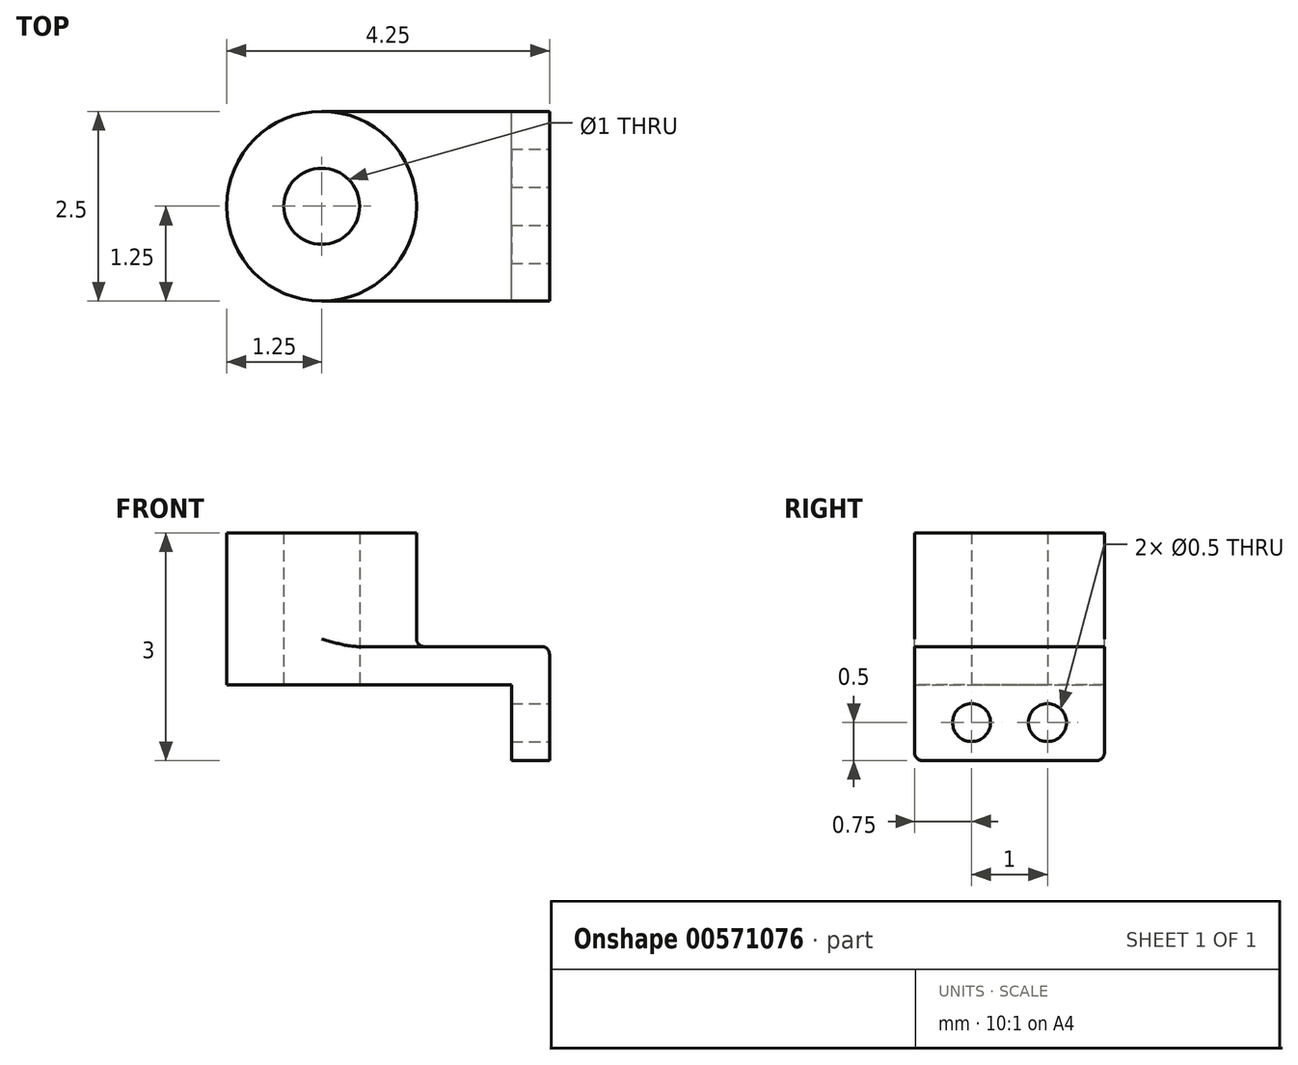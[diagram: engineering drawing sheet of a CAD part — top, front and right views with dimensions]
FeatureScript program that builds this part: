
annotation { "Feature Type Name" : "Feature", "Feature Type Description" : "" }
export const myFeature = defineFeature(function(context is Context, id is Id, definition is map)
    precondition{}
    {
        {
            var Q0;
            Q0=qCreatedBy(makeId("Top.planeOp"),FACE);
            var sketch = newSketch(context, id + "F0", { "sketchPlane" : qUnion([Q0])});
            skLineSegment(sketch, "E0.bottom", {"start": v(1.5, -1.25) * mm, "end": v(-1.5, -1.25) * mm});
            skLineSegment(sketch, "E0.top", {"start": v(1.5, 1.25) * mm, "end": v(-1.5, 1.25) * mm});
            skLineSegment(sketch, "E0.left", {"start": v(1.5, -1.25) * mm, "end": v(1.5, 1.25) * mm});
            skLineSegment(sketch, "E0.right", {"start": v(-1.5, -1.25) * mm, "end": v(-1.5, 1.25) * mm});
            skPoint(sketch, "E0.middle", {"position": v(0, 0) * mm});
            skCircle(sketch, "E1", {"center": v(-1.5, 0) * mm, "radius": 1.25 * mm});
            skCircle(sketch, "E2", {"center": v(-1.5, 0) * mm, "radius": 0.5 * mm});
            skSolve(sketch);
        }
        {
            var Q0;
            Q0 = qSketchRegion(id + "F0", true);
            extrude(context, id + "F1", {"entities" : qUnion([Q0]), "depth" : 0.5 * mm, "offsetDistance" : 25 * mm});
        }
        {
            var Q0;
            {var subQ1=sQuery(id+"F0.wireOp",EDGE,"E0.right");var subQ3=sQuery(id+"F0.wireOp",EDGE,"E2");var subQ4=makeQuery(id+"F0.imprint","INTERSECT",VERTEX,{"disambiguationData":[OD(0.0)],"derivedFrom":[subQ1,subQ3]});Q0=makeQuery(id+"F0.imprint","IMPRINT",FACE,{"disambiguationData":[TD([[makeQuery(id+"F0.imprint","IMPRINT",EDGE,{"disambiguationData":[TD([[subQ4,1.0]])],"derivedFrom":subQ3}),-1.0]])]});}
            var Q1;
            {var subQ1=sQuery(id+"F0.wireOp",EDGE,"E0.right");var subQ3=sQuery(id+"F0.wireOp",EDGE,"E2");var subQ4=makeQuery(id+"F0.imprint","INTERSECT",VERTEX,{"disambiguationData":[OD(0.0)],"derivedFrom":[subQ1,subQ3]});Q1=makeQuery(id+"F0.imprint","IMPRINT",FACE,{"disambiguationData":[TD([[makeQuery(id+"F0.imprint","IMPRINT",EDGE,{"disambiguationData":[TD([[subQ4,-1.0]])],"derivedFrom":subQ3}),-1.0]])]});}
            extrude(context, id + "F2", {"entities" : qUnion([Q0, Q1]), "operationType" : NewBodyOperationType.ADD, "depth" : 2 * mm, "offsetDistance" : 25 * mm});
        }
        {
            var Q0;
            Q0=makeQuery(id+"F1.opExtrude","SWEPT_FACE",FACE,{"disambiguationData":[OSD([sQuery(id+"F0.wireOp",EDGE,"E0.left")])]});
            var sketch = newSketch(context, id + "F3", { "sketchPlane" : qUnion([Q0])});
            skLineSegment(sketch, "E3.bottom", {"start": v(-1.25, 0.5) * mm, "end": v(1.25, 0.5) * mm});
            skLineSegment(sketch, "E3.top", {"start": v(-1.25, -1) * mm, "end": v(1.25, -1) * mm});
            skLineSegment(sketch, "E3.left", {"start": v(-1.25, 0.5) * mm, "end": v(-1.25, -1) * mm});
            skLineSegment(sketch, "E3.right", {"start": v(1.25, 0.5) * mm, "end": v(1.25, -1) * mm});
            skLineSegment(sketch, "E4", {"start": v(0, 0.5) * mm, "end": v(0, -1) * mm, "construction": true});
            skCircle(sketch, "E5", {"center": v(-0.5, -0.5) * mm, "radius": 0.25 * mm});
            skCircle(sketch, "E6.MirrorC", {"center": v(0.5, -0.5) * mm, "radius": 0.25 * mm});
            skSolve(sketch);
        }
        {
            var Q0;
            Q0 = qSketchRegion(id + "F3", true);
            extrude(context, id + "F4", {"entities" : qUnion([Q0]), "operationType" : NewBodyOperationType.ADD, "oppositeDirection" : true, "depth" : .5 * mm, "offsetDistance" : 25 * mm});
        }
        {
            var Q0;
            {var subQ0=sQuery(id+"F0.wireOp",EDGE,"E1");Q0=makeQuery(id+"F2.boolean.opBoolean","INTERSECT",EDGE,{"derivedFrom":[makeQuery(id+"F1.opExtrude","CAP_FACE",FACE,{"disambiguationData":[OSD([sQuery(id+"F0.wireOp",EDGE,"E0.bottom"),sQuery(id+"F0.wireOp",EDGE,"E0.top"),sQuery(id+"F0.wireOp",EDGE,"E0.left"),subQ0,sQuery(id+"F0.wireOp",EDGE,"E2")])],"isStart":false}),makeQuery(id+"F2.opExtrude","SWEPT_FACE",FACE,{"disambiguationData":[OSD([subQ0])]})]});}
            var Q1;
            Q1=makeQuery(id+"F1.opExtrude","CAP_EDGE",EDGE,{"disambiguationData":[OSD([sQuery(id+"F0.wireOp",EDGE,"E0.left")])],"isStart":false});
            var Q2;
            Q2=makeQuery(id+"F4.opExtrude","SWEPT_EDGE",EDGE,{"disambiguationData":[OSD([sQuery(id+"F3.wireOp",EDGE,"E3.top"),sQuery(id+"F3.wireOp",EDGE,"E3.left")])]});
            var Q3;
            Q3=makeQuery(id+"F4.opExtrude","SWEPT_EDGE",EDGE,{"disambiguationData":[OSD([sQuery(id+"F3.wireOp",EDGE,"E3.top"),sQuery(id+"F3.wireOp",EDGE,"E3.right")])]});
            fillet(context, id + "F5", {"entities" : qUnion([Q0, Q1, Q2, Q3]), "radius" : 0.1 * mm, "tangentPropagation" : true, "allowEdgeOverflow" : false});
        }
    });
